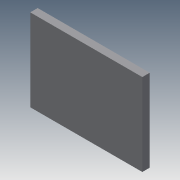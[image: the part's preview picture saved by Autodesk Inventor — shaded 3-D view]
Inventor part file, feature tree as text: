
AUTODESK INVENTOR PART (.ipt)
format: ipt  version: 2015 (Build 190159000, 159)  size: 69,120 bytes
history: native  units: mm
features: extrude x1, sketch x1
ambient origin geometry x8: Origin, YZ Plane, XZ Plane, XY Plane, X Axis, Y Axis, Z Axis, Center Point
bodies: Solid1 (feature_tree)
feature tree (2):
  extrude  "Extrusion1"  Depth=150.0mm
  sketch  "Sketch1"  dims[d0=110.0mm d1=150.0mm d2=10.0mm d3=0.0mm]
